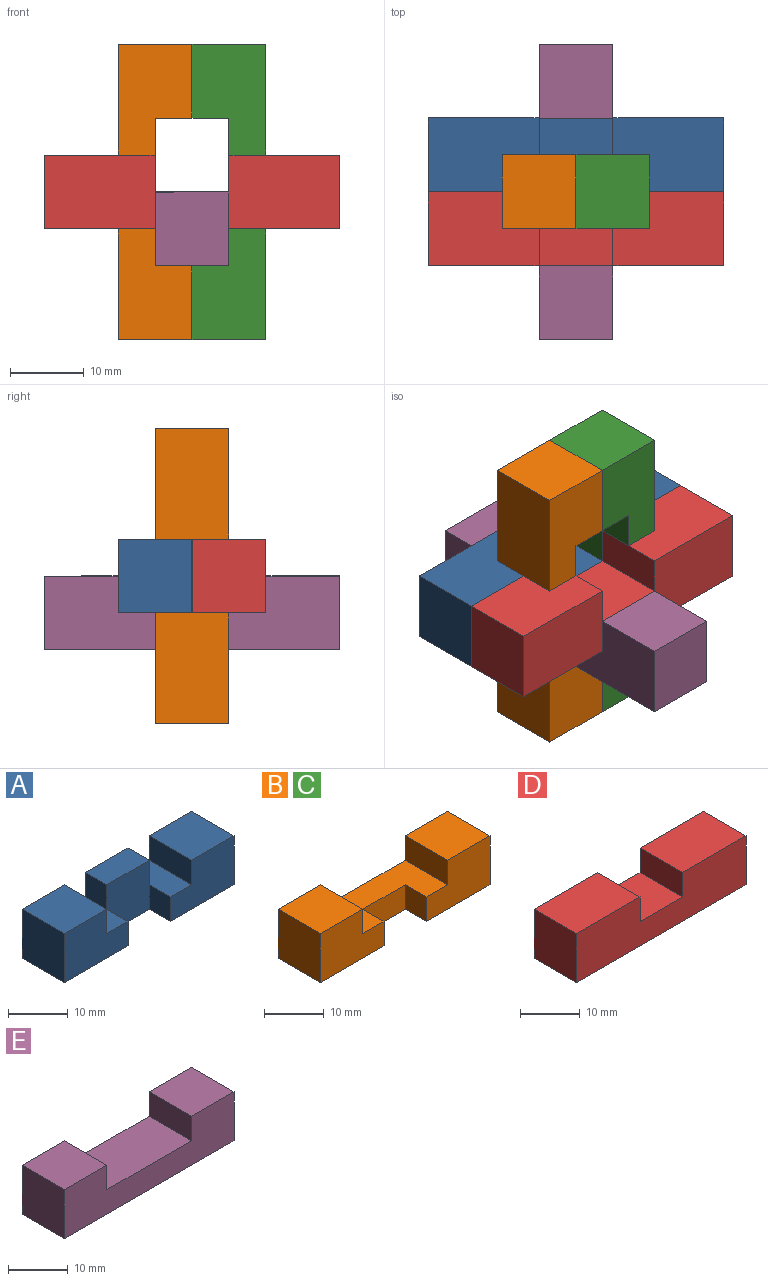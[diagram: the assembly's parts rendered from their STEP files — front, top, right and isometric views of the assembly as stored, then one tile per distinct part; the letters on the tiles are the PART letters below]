
ASSEMBLY  parts=5 mates=4
PART A: 18 faces, bbox 40x10x10 mm
  f0: plane 10x5mm, normal (0,0,1), area 50mm2, adj f1,f5,f11,f12,f16
  f1: plane 15x10mm, normal (0,-1,0), area 125mm2, adj f0,f2,f4,f7,f11,f12
  f2: plane 40x10mm, normal (0,0,-1), area 350mm2, adj f1,f3,f5,f6,f7,f12,f13,f14
  f3: plane 15x10mm, normal (0,-1,0), area 125mm2, adj f2,f6,f8,f9,f10,f13
  f4: plane 10x10mm, normal (0,0,1), area 100mm2, adj f1,f5,f7,f11
  f5: plane 40x10mm, normal (0,1,0), area 350mm2, adj f0,f2,f4,f6,f7,f8,f9,f10
  f6: plane 10x10mm, normal (-1,0,0), area 100mm2, adj f2,f3,f5,f8
  f7: plane 10x10mm, normal (1,0,0), area 100mm2, adj f1,f2,f4,f5
  f8: plane 10x10mm, normal (0,0,1), area 100mm2, adj f3,f5,f6,f9
  f9: plane 10x5mm, normal (1,0,0), area 50mm2, adj f3,f5,f8,f10
  f10: plane 10x5mm, normal (0,0,1), area 50mm2, adj f3,f5,f9,f13,f15
  f11: plane 10x5mm, normal (-1,0,0), area 50mm2, adj f0,f1,f4,f5
  f12: plane 5x5mm, normal (-1,0,0), area 25mm2, adj f0,f1,f2,f14
  f13: plane 5x5mm, normal (1,0,0), area 25mm2, adj f2,f3,f10,f14
  f14: plane 10x10mm, normal (0,-1,0), area 100mm2, adj f2,f12,f13,f15,f16,f17
  f15: plane 5x5mm, normal (-1,0,0), area 25mm2, adj f5,f10,f14,f17
  f16: plane 5x5mm, normal (1,0,0), area 25mm2, adj f0,f5,f14,f17
  f17: plane 10x5mm, normal (0,0,1), area 50mm2, adj f5,f14,f15,f16
PART B: 14 faces, bbox 40x10x10 mm
  f0: plane 15x10mm, normal (0,-1,0), area 125mm2, adj f1,f3,f6,f9,f10,f11
  f1: plane 40x10mm, normal (0,0,-1), area 350mm2, adj f0,f2,f4,f5,f6,f11,f12,f13
  f2: plane 15x10mm, normal (0,-1,0), area 125mm2, adj f1,f5,f7,f8,f9,f12
  f3: plane 10x10mm, normal (0,0,1), area 100mm2, adj f0,f4,f6,f10
  f4: plane 40x10mm, normal (0,1,0), area 300mm2, adj f1,f3,f5,f6,f7,f8,f9,f10
  f5: plane 10x10mm, normal (-1,0,0), area 100mm2, adj f1,f2,f4,f7
  f6: plane 10x10mm, normal (1,0,0), area 100mm2, adj f0,f1,f3,f4
  f7: plane 10x10mm, normal (0,0,1), area 100mm2, adj f2,f4,f5,f8
  f8: plane 10x5mm, normal (1,0,0), area 50mm2, adj f2,f4,f7,f9
  f9: plane 20x10mm, normal (0,0,1), area 150mm2, adj f0,f2,f4,f8,f10,f11,f12,f13
  f10: plane 10x5mm, normal (-1,0,0), area 50mm2, adj f0,f3,f4,f9
  f11: plane 5x5mm, normal (-1,0,0), area 25mm2, adj f0,f1,f9,f13
  f12: plane 5x5mm, normal (1,0,0), area 25mm2, adj f1,f2,f9,f13
  f13: plane 10x5mm, normal (0,-1,0), area 50mm2, adj f1,f9,f11,f12
PART C: same geometry as B
PART D: 10 faces, bbox 40x10x10 mm
  f0: plane 40x10mm, normal (0,-1,0), area 350mm2, adj f1,f3,f4,f5,f6,f7,f8,f9
  f1: plane 15x10mm, normal (0,0,1), area 150mm2, adj f0,f2,f4,f9
  f2: plane 40x10mm, normal (0,1,0), area 350mm2, adj f1,f3,f4,f5,f6,f7,f8,f9
  f3: plane 10x10mm, normal (-1,0,0), area 100mm2, adj f0,f2,f5,f6
  f4: plane 10x10mm, normal (1,0,0), area 100mm2, adj f0,f1,f2,f6
  f5: plane 15x10mm, normal (0,0,1), area 150mm2, adj f0,f2,f3,f7
  f6: plane 40x10mm, normal (0,0,-1), area 400mm2, adj f0,f2,f3,f4
  f7: plane 10x5mm, normal (1,0,0), area 50mm2, adj f0,f2,f5,f8
  f8: plane 10x10mm, normal (0,0,1), area 100mm2, adj f0,f2,f7,f9
  f9: plane 10x5mm, normal (-1,0,0), area 50mm2, adj f0,f1,f2,f8
PART E: 10 faces, bbox 40x10x10 mm
  f0: plane 40x10mm, normal (0,-1,0), area 300mm2, adj f1,f3,f4,f5,f6,f7,f8,f9
  f1: plane 10x10mm, normal (0,0,1), area 100mm2, adj f0,f2,f4,f9
  f2: plane 40x10mm, normal (0,1,0), area 300mm2, adj f1,f3,f4,f5,f6,f7,f8,f9
  f3: plane 10x10mm, normal (-1,0,0), area 100mm2, adj f0,f2,f5,f6
  f4: plane 10x10mm, normal (1,0,0), area 100mm2, adj f0,f1,f2,f6
  f5: plane 10x10mm, normal (0,0,1), area 100mm2, adj f0,f2,f3,f7
  f6: plane 40x10mm, normal (0,0,-1), area 400mm2, adj f0,f2,f3,f4
  f7: plane 10x5mm, normal (1,0,0), area 50mm2, adj f0,f2,f5,f8
  f8: plane 20x10mm, normal (0,0,1), area 200mm2, adj f0,f2,f7,f9
  f9: plane 10x5mm, normal (-1,0,0), area 50mm2, adj f0,f1,f2,f8
PLACE A rot(axis=(0,0.71,-0.71),180deg) t=(-5,30,-10)mm
PLACE B rot(axis=(0,1,0),90deg) t=(-15,20,-10)mm
PLACE C rot(axis=(0,-1,0),90deg) t=(5,20,-10)mm fixed
PLACE D t=(-5,15,-15)mm
PLACE E rot(axis=(0,0,1),90deg) t=(-5,20,-20)mm fixed
MATE slider B.f4 <-> E.f3  axis (0,1,0) through (-5,25,-20)mm
MATE slider D.f3 <-> C.f1  axis (-1,0,0) through (-25,20,-10)mm
MATE fastened B.f7 <-> C.f3  axis (1,0,0) through (-5,20,5)mm
MATE fastened A.f2 <-> E.f9  axis (0,1,0) through (-5,30,-10)mm
